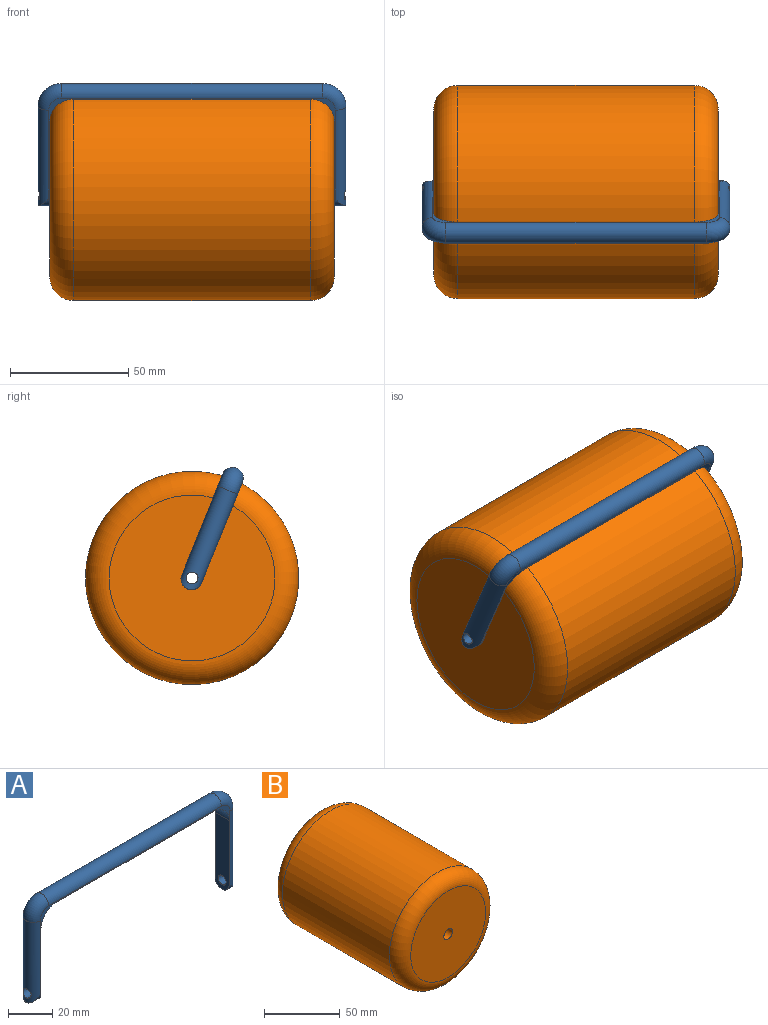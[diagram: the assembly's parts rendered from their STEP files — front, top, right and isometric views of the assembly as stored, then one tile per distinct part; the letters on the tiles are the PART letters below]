
ASSEMBLY  parts=2 mates=1
PART A: 16 faces, bbox 131.6x9x55.8 mm
  f0: plane 40x9mm, normal (1,0,0), area 331.7mm2, adj f3,f4,f5,f8,f14
  f1: plane 100x9mm, normal (0,0,-1), area 900mm2, adj f3,f4,f5,f6
  f2: plane 40x9mm, normal (-1,0,0), area 331.7mm2, adj f3,f4,f6,f7,f9
  f3: plane 121x46mm, normal (0,-1,0), area 135.9mm2, adj f0,f1,f2,f5,f6,f9,f10,f11
  f4: plane 121x46mm, normal (0,1,0), area 135.9mm2, adj f0,f1,f2,f5,f6,f9,f10,f11
  f5: cylinder r=10mm len=10mm, axis (0,-1,0), area 141.4mm2, adj f0,f1,f3,f4
  f6: cylinder r=10mm len=10mm, axis (0,1,0), area 141.4mm2, adj f1,f2,f3,f4
  f7: cylinder r=2.5mm len=5mm, axis (1,0,0), area 72.7mm2, adj f2,f10
  f8: cylinder r=2.5mm len=5mm, axis (1,0,0), area 72.7mm2, adj f0,f15
  f9: cylinder r=4.5mm len=9mm, axis (1,0,0), area 47.6mm2, adj f2,f3,f4,f10
  f10: cylinder r=4.5mm len=45.02mm, axis (0,0,1), area 592.6mm2, adj f3,f4,f7,f9,f11
  f11: torus R=5.5mm, axis (0,-1,0), area 185.8mm2, adj f3,f4,f10,f12
  f12: cylinder r=4.5mm len=110mm, axis (-1,0,0), area 1555.1mm2, adj f3,f4,f11,f13
  f13: torus R=5.5mm, axis (0,-1,0), area 185.8mm2, adj f3,f4,f12,f15
  f14: cylinder r=4.5mm len=9mm, axis (1,0,0), area 47.6mm2, adj f0,f3,f4,f15
  f15: cylinder r=4.5mm len=45.02mm, axis (0,0,-1), area 592.6mm2, adj f3,f4,f8,f13,f14
PART B: 6 faces, bbox 97.4x120x97.4 mm
  f0: cylinder r=45mm len=100mm, axis (0,1,0), area 28274.3mm2, adj f3,f4
  f1: plane 70x70mm, normal (0,-1,0), area 3798.2mm2, adj f4,f5
  f2: plane 70x70mm, normal (0,1,0), area 3798.2mm2, adj f3,f5
  f3: torus R=35mm, axis (0,-1,0), area 4082.7mm2, adj f0,f2
  f4: torus R=35mm, axis (0,-1,0), area 4082.7mm2, adj f0,f1
  f5: cylinder r=4mm len=120mm, axis (0,-1,0), area 3015.9mm2, adj f1,f2
PLACE A rot(axis=(1,0,0),22.1deg) t=(-1.95,12.24,25.84)mm
PLACE B rot(axis=(0.58,0.58,-0.58),120deg) t=(-1.95,12.24,25.84)mm fixed
MATE revolute B.f5 <-> A.f7  axis (-1,0,0) through (-61.95,12.24,25.84)mm
